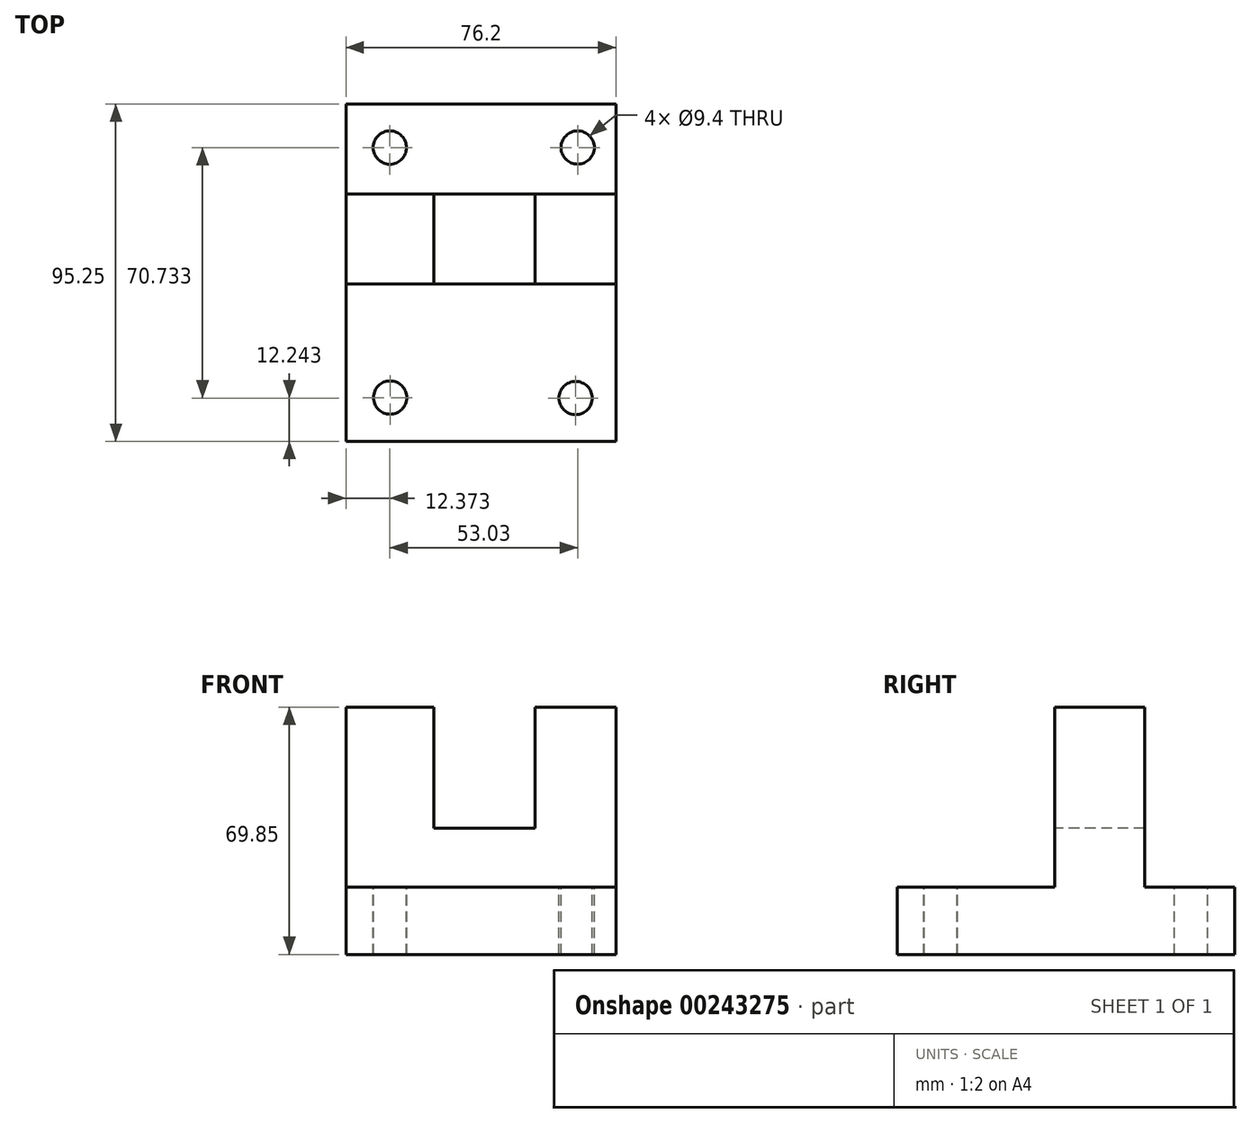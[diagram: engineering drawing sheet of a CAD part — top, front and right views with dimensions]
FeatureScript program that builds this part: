
annotation { "Feature Type Name" : "Feature", "Feature Type Description" : "" }
export const myFeature = defineFeature(function(context is Context, id is Id, definition is map)
    precondition{}
    {
        {
            var Q0;
            Q0=qCreatedBy(makeId("Right.planeOp"),FACE);
            var sketch = newSketch(context, id + "F0", { "sketchPlane" : qUnion([Q0])});
            skLineSegment(sketch, "E0", {"start": v(-28.85, -19.05) * mm, "end": v(66.4, -19.05) * mm});
            skLineSegment(sketch, "E1", {"start": v(-28.85, -19.05) * mm, "end": v(-28.85, 0) * mm});
            skLineSegment(sketch, "E2", {"start": v(-28.85, 0) * mm, "end": v(15.6, 0) * mm});
            skLineSegment(sketch, "E3", {"start": v(15.6, 0) * mm, "end": v(15.6, 50.8) * mm});
            skLineSegment(sketch, "E4", {"start": v(15.6, 50.8) * mm, "end": v(41, 50.8) * mm});
            skLineSegment(sketch, "E5", {"start": v(41, 50.8) * mm, "end": v(41, 0) * mm});
            skLineSegment(sketch, "E6", {"start": v(41, 0) * mm, "end": v(66.4, 0) * mm});
            skLineSegment(sketch, "E7", {"start": v(66.4, -19.05) * mm, "end": v(66.4, 0) * mm});
            skSolve(sketch);
        }
        {
            var Q0;
            Q0=makeQuery(id+"F0.imprint","IMPRINT",FACE,{"disambiguationData":[TD([[makeQuery(id+"F0.imprint","IMPRINT",EDGE,{"derivedFrom":sQuery(id+"F0.wireOp",EDGE,"E0")}),1.0]])]});
            extrude(context, id + "F1", {"entities" : qUnion([Q0]), "depth" : 76.2 * mm});
        }
        {
            var Q0;
            Q0=makeQuery(id+"F1.opExtrude","SWEPT_FACE",FACE,{"disambiguationData":[OSD([sQuery(id+"F0.wireOp",EDGE,"E3")])]});
            var sketch = newSketch(context, id + "F2", { "sketchPlane" : qUnion([Q0])});
            skLineSegment(sketch, "E8.bottom", {"start": v(24.82, 50.8) * mm, "end": v(53.4, 50.8) * mm});
            skLineSegment(sketch, "E8.top", {"start": v(24.82, 16.6) * mm, "end": v(53.4, 16.6) * mm});
            skLineSegment(sketch, "E8.left", {"start": v(24.82, 50.8) * mm, "end": v(24.82, 16.6) * mm});
            skLineSegment(sketch, "E8.right", {"start": v(53.4, 50.8) * mm, "end": v(53.4, 16.6) * mm});
            skSolve(sketch);
        }
        {
            var Q0;
            Q0=makeQuery(id+"F2.imprint","IMPRINT",FACE,{"disambiguationData":[TD([[makeQuery(id+"F2.imprint","IMPRINT",EDGE,{"derivedFrom":sQuery(id+"F2.wireOp",EDGE,"E8.bottom")}),1.0]])]});
            extrude(context, id + "F3", {"entities" : qUnion([Q0]), "operationType" : NewBodyOperationType.REMOVE, "oppositeDirection" : true, "depth" : 33.78 * mm});
        }
        {
            var Q0;
            Q0=makeQuery(id+"F1.opExtrude","SWEPT_FACE",FACE,{"disambiguationData":[OSD([sQuery(id+"F0.wireOp",EDGE,"E6")])]});
            var sketch = newSketch(context, id + "F4", { "sketchPlane" : qUnion([Q0])});
            skCircle(sketch, "E9", {"center": v(64.81, -16.6) * mm, "radius": 4.7 * mm});
            skCircle(sketch, "E10", {"center": v(12.46, -16.47) * mm, "radius": 4.7 * mm});
            skCircle(sketch, "E11", {"center": v(12.37, 54.12) * mm, "radius": 4.7 * mm});
            skCircle(sketch, "E12", {"center": v(65.4, 54.13) * mm, "radius": 4.7 * mm});
            skSolve(sketch);
        }
        {
            var Q0;
            Q0=makeQuery(id+"F4.imprint","IMPRINT",FACE,{"disambiguationData":[TD([[makeQuery(id+"F4.imprint","IMPRINT",EDGE,{"derivedFrom":sQuery(id+"F4.wireOp",EDGE,"E11")}),1.0]])]});
            var Q1;
            Q1=makeQuery(id+"F4.imprint","IMPRINT",FACE,{"disambiguationData":[TD([[makeQuery(id+"F4.imprint","IMPRINT",EDGE,{"derivedFrom":sQuery(id+"F4.wireOp",EDGE,"E12")}),1.0]])]});
            var Q2;
            Q2=makeQuery(id+"F4.imprint","IMPRINT",FACE,{"disambiguationData":[TD([[makeQuery(id+"F4.imprint","IMPRINT",EDGE,{"derivedFrom":sQuery(id+"F4.wireOp",EDGE,"E10")}),1.0]])]});
            var Q3;
            Q3=makeQuery(id+"F4.imprint","IMPRINT",FACE,{"disambiguationData":[TD([[makeQuery(id+"F4.imprint","IMPRINT",EDGE,{"derivedFrom":sQuery(id+"F4.wireOp",EDGE,"E9")}),1.0]])]});
            extrude(context, id + "F5", {"entities" : qUnion([Q0, Q1, Q2, Q3]), "operationType" : NewBodyOperationType.REMOVE, "oppositeDirection" : true, "depth" : 53.6 * mm});
        }
    });
